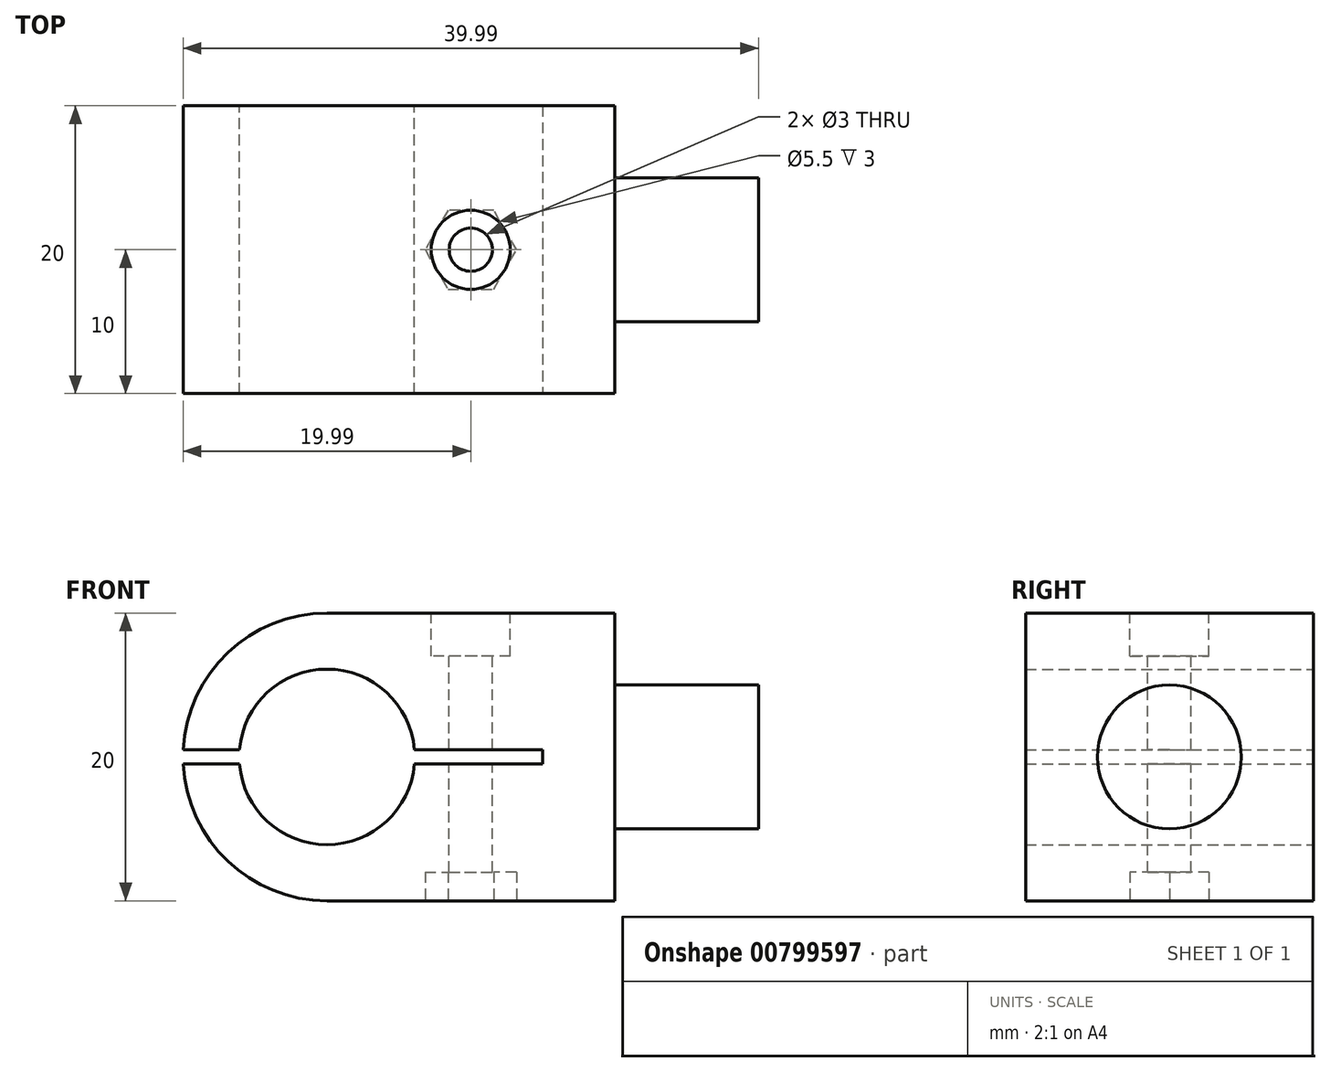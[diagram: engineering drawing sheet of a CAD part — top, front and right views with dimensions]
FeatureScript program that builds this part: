
annotation { "Feature Type Name" : "Feature", "Feature Type Description" : "" }
export const myFeature = defineFeature(function(context is Context, id is Id, definition is map)
    precondition{}
    {
        {
            var Q0;
            Q0=qCreatedBy(makeId("Front.planeOp"),FACE);
            var sketch = newSketch(context, id + "F0", { "sketchPlane" : qUnion([Q0])});
            skCircle(sketch, "E0", {"center": v(0, 0) * mm, "radius": 10 * mm});
            skLineSegment(sketch, "E1", {"start": v(0, 10) * mm, "end": v(20, 10) * mm});
            skLineSegment(sketch, "E2", {"start": v(20, 10) * mm, "end": v(20, -10) * mm});
            skLineSegment(sketch, "E3", {"start": v(20, -10) * mm, "end": v(0, -10) * mm});
            skCircle(sketch, "E4", {"center": v(0, 0) * mm, "radius": 6.1 * mm});
            skSolve(sketch);
        }
        {
            var Q0;
            {var subQ0=sQuery(id+"F0.wireOp",EDGE,"E1");Q0=makeQuery(id+"F0.imprint","IMPRINT",FACE,{"disambiguationData":[TD([[makeQuery(id+"F0.imprint","IMPRINT",EDGE,{"derivedFrom":subQ0}),-1.0]])]});}
            var Q1;
            Q1=makeQuery(id+"F0.imprint","IMPRINT",FACE,{"disambiguationData":[TD([[makeQuery(id+"F0.imprint","IMPRINT",EDGE,{"derivedFrom":sQuery(id+"F0.wireOp",EDGE,"E4")}),-1.0]])]});
            extrude(context, id + "F1", {"entities" : qUnion([Q0, Q1]), "depth" : 20 * mm, "offsetDistance" : 25 * mm});
        }
        {
            var Q0;
            Q0=makeQuery(id+"F1.opExtrude","CAP_FACE",FACE,{"disambiguationData":[OSD([sQuery(id+"F0.wireOp",EDGE,"E0"),sQuery(id+"F0.wireOp",EDGE,"E1"),sQuery(id+"F0.wireOp",EDGE,"E2"),sQuery(id+"F0.wireOp",EDGE,"E3"),sQuery(id+"F0.wireOp",EDGE,"E4")])],"isStart":false});
            var sketch = newSketch(context, id + "F2", { "sketchPlane" : qUnion([Q0])});
            skLineSegment(sketch, "E5.bottom", {"start": v(-17.84, 0.5) * mm, "end": v(15, 0.5) * mm});
            skLineSegment(sketch, "E5.top", {"start": v(-17.84, -0.5) * mm, "end": v(15, -0.5) * mm});
            skLineSegment(sketch, "E5.left", {"start": v(-17.84, 0.5) * mm, "end": v(-17.84, -0.5) * mm});
            skLineSegment(sketch, "E5.right", {"start": v(15, 0.5) * mm, "end": v(15, -0.5) * mm});
            skSolve(sketch);
        }
        {
            var Q0;
            Q0=makeQuery(id+"F1.opExtrude","SWEPT_FACE",FACE,{"disambiguationData":[OSD([sQuery(id+"F0.wireOp",EDGE,"E1")])]});
            var sketch = newSketch(context, id + "F3", { "sketchPlane" : qUnion([Q0])});
            skPoint(sketch, "E6", {"position": v(10, -10) * mm});
            skCircle(sketch, "E7", {"center": v(10, -10) * mm, "radius": 1.5 * mm});
            skSolve(sketch);
        }
        {
            var Q0;
            Q0=makeQuery(id+"F3.imprint","IMPRINT",FACE,{"disambiguationData":[TD([[makeQuery(id+"F3.imprint","IMPRINT",EDGE,{"derivedFrom":sQuery(id+"F3.wireOp",EDGE,"E7")}),1.0]])]});
            extrude(context, id + "F4", {"entities" : qUnion([Q0]), "operationType" : NewBodyOperationType.REMOVE, "oppositeDirection" : true, "depth" : 25 * mm, "offsetDistance" : 25 * mm});
        }
        {
            var Q0;
            {var subQ0=sQuery(id+"F2.wireOp",EDGE,"E5.left");Q0=makeQuery(id+"F2.imprint","IMPRINT",FACE,{"disambiguationData":[TD([[makeQuery(id+"F2.imprint","IMPRINT",EDGE,{"derivedFrom":subQ0}),1.0]])]});}
            var Q1;
            {var subQ0=sQuery(id+"F2.wireOp",EDGE,"E5.bottom");var subQ1=makeQuery(id+"F1.opExtrude","CAP_EDGE",EDGE,{"disambiguationData":[OSD([sQuery(id+"F0.wireOp",EDGE,"E0")])],"isStart":false});var subQ2=makeQuery(id+"F2.imprint","INTERSECT",VERTEX,{"derivedFrom":[subQ1,subQ0]});Q1=makeQuery(id+"F2.imprint","IMPRINT",FACE,{"disambiguationData":[TD([[makeQuery(id+"F2.imprint","IMPRINT",EDGE,{"disambiguationData":[TD([[subQ2,-1.0]])],"derivedFrom":subQ0}),-1.0]])]});}
            var Q2;
            {var subQ0=sQuery(id+"F2.wireOp",EDGE,"E5.bottom");var subQ1=makeQuery(id+"F1.opExtrude","CAP_EDGE",EDGE,{"disambiguationData":[OSD([sQuery(id+"F0.wireOp",EDGE,"E4")])],"isStart":false});var subQ2=makeQuery(id+"F2.imprint","INTERSECT",VERTEX,{"disambiguationData":[OD(0.0)],"derivedFrom":[subQ1,subQ0]});Q2=makeQuery(id+"F2.imprint","IMPRINT",FACE,{"disambiguationData":[TD([[makeQuery(id+"F2.imprint","IMPRINT",EDGE,{"disambiguationData":[TD([[subQ2,-1.0]])],"derivedFrom":subQ0}),-1.0]])]});}
            var Q3;
            {var subQ0=sQuery(id+"F2.wireOp",EDGE,"E5.right");Q3=makeQuery(id+"F2.imprint","IMPRINT",FACE,{"disambiguationData":[TD([[makeQuery(id+"F2.imprint","IMPRINT",EDGE,{"derivedFrom":subQ0}),-1.0]])]});}
            extrude(context, id + "F5", {"entities" : qUnion([Q0, Q1, Q2, Q3]), "operationType" : NewBodyOperationType.REMOVE, "oppositeDirection" : true, "depth" : 25 * mm, "offsetDistance" : 25 * mm});
        }
        {
            var Q0;
            Q0=makeQuery(id+"F1.opExtrude","SWEPT_FACE",FACE,{"disambiguationData":[OSD([sQuery(id+"F0.wireOp",EDGE,"E2")])]});
            var sketch = newSketch(context, id + "F6", { "sketchPlane" : qUnion([Q0])});
            skPoint(sketch, "E8", {"position": v(-10, 0) * mm});
            skCircle(sketch, "E9", {"center": v(-10, 0) * mm, "radius": 5 * mm});
            skSolve(sketch);
        }
        {
            var Q0;
            Q0=makeQuery(id+"F6.imprint","IMPRINT",FACE,{"disambiguationData":[TD([[makeQuery(id+"F6.imprint","IMPRINT",EDGE,{"derivedFrom":sQuery(id+"F6.wireOp",EDGE,"E9")}),1.0]])]});
            extrude(context, id + "F7", {"entities" : qUnion([Q0]), "operationType" : NewBodyOperationType.ADD, "depth" : 10 * mm, "offsetDistance" : 25 * mm});
        }
        {
            var Q0;
            Q0=makeQuery(id+"F1.opExtrude","SWEPT_FACE",FACE,{"disambiguationData":[OSD([sQuery(id+"F0.wireOp",EDGE,"E1")])]});
            var sketch = newSketch(context, id + "F8", { "sketchPlane" : qUnion([Q0])});
            skCircle(sketch, "E10", {"center": v(10, -10) * mm, "radius": 2.75 * mm});
            skSolve(sketch);
        }
        {
            var Q0;
            Q0=makeQuery(id+"F8.imprint","IMPRINT",FACE,{"disambiguationData":[TD([[makeQuery(id+"F8.imprint","IMPRINT",EDGE,{"derivedFrom":sQuery(id+"F8.wireOp",EDGE,"E10")}),1.0]])]});
            extrude(context, id + "F9", {"entities" : qUnion([Q0]), "operationType" : NewBodyOperationType.REMOVE, "oppositeDirection" : true, "depth" : 3 * mm, "offsetDistance" : 25 * mm});
        }
        {
            var Q0;
            Q0=makeQuery(id+"F1.opExtrude","SWEPT_FACE",FACE,{"disambiguationData":[OSD([sQuery(id+"F0.wireOp",EDGE,"E3")])]});
            var sketch = newSketch(context, id + "F10", { "sketchPlane" : qUnion([Q0])});
            skCircle(sketch, "E11.cCircle", {"center": v(10, 10) * mm, "radius": 2.75 * mm, "construction": true});
            skLineSegment(sketch, "E11.0", {"start": v(8.41, 12.75) * mm, "end": v(11.59, 12.75) * mm});
            skLineSegment(sketch, "E11.1", {"start": v(11.59, 12.75) * mm, "end": v(13.18, 10) * mm});
            skLineSegment(sketch, "E11.2", {"start": v(13.18, 10) * mm, "end": v(11.59, 7.25) * mm});
            skLineSegment(sketch, "E11.3", {"start": v(11.59, 7.25) * mm, "end": v(8.41, 7.25) * mm});
            skLineSegment(sketch, "E11.4", {"start": v(8.41, 7.25) * mm, "end": v(6.82, 10) * mm});
            skLineSegment(sketch, "E11.5", {"start": v(6.82, 10) * mm, "end": v(8.41, 12.75) * mm});
            skPoint(sketch, "E11.0.midPoint", {"position": v(10, 12.75) * mm});
            skSolve(sketch);
        }
        {
            var Q0;
            Q0=makeQuery(id+"F10.imprint","IMPRINT",FACE,{"disambiguationData":[TD([[makeQuery(id+"F10.imprint","IMPRINT",EDGE,{"derivedFrom":sQuery(id+"F10.wireOp",EDGE,"E11.0")}),-1.0]])]});
            extrude(context, id + "F11", {"entities" : qUnion([Q0]), "operationType" : NewBodyOperationType.REMOVE, "oppositeDirection" : true, "depth" : 2 * mm, "offsetDistance" : 25 * mm});
        }
    });
